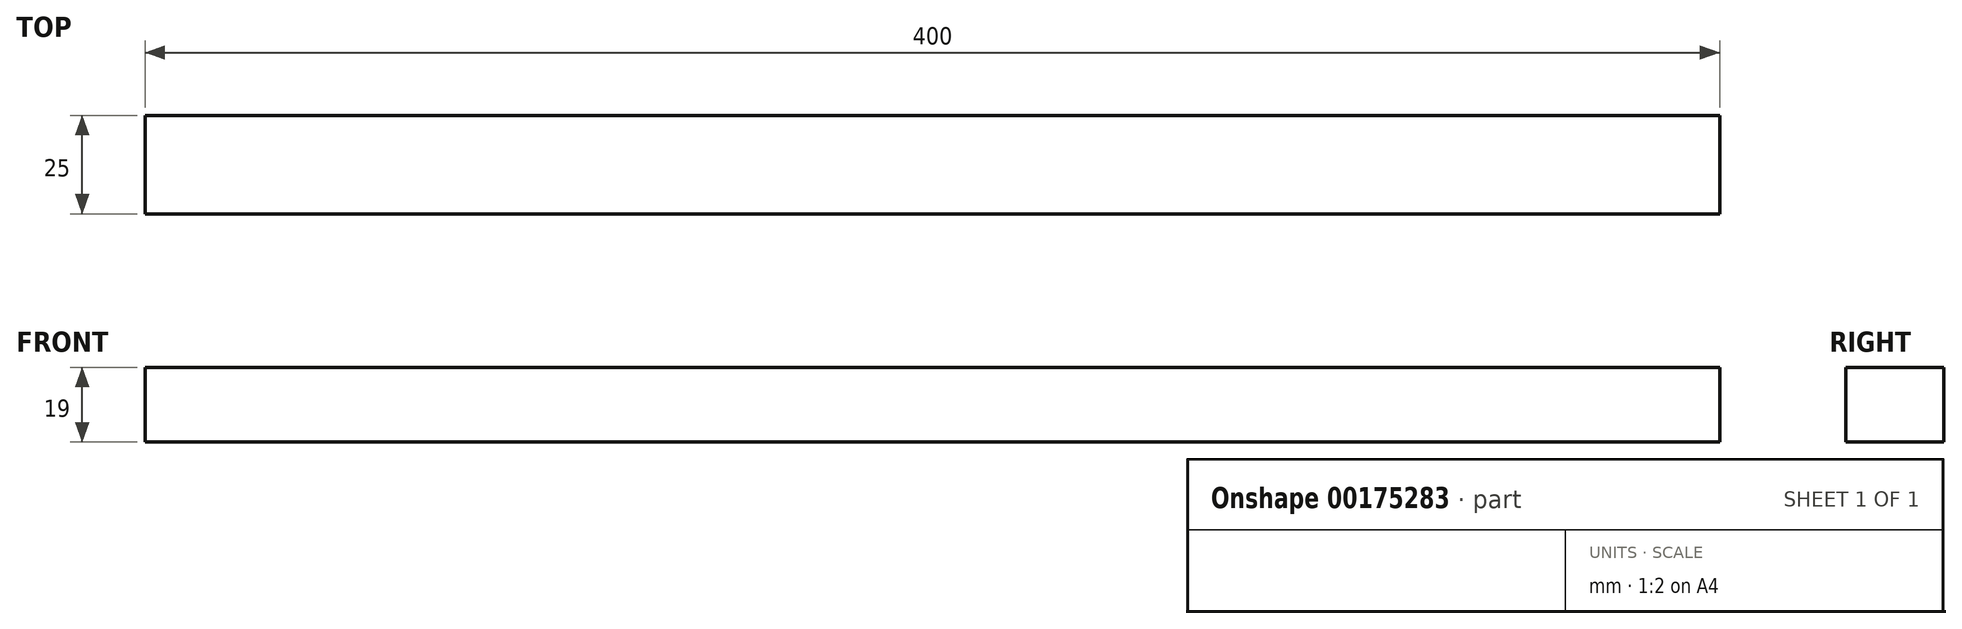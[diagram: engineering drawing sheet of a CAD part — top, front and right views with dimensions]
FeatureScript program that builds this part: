
annotation { "Feature Type Name" : "Feature", "Feature Type Description" : "" }
export const myFeature = defineFeature(function(context is Context, id is Id, definition is map)
    precondition{}
    {
        {
            var Q0;
            Q0=qCreatedBy(makeId("Front.planeOp"),FACE);
            var sketch = newSketch(context, id + "F0", { "sketchPlane" : qUnion([Q0])});
            skLineSegment(sketch, "E0.bottom", {"start": v(-200, 9.5) * mm, "end": v(200, 9.5) * mm});
            skLineSegment(sketch, "E0.top", {"start": v(-200, -9.5) * mm, "end": v(200, -9.5) * mm});
            skLineSegment(sketch, "E0.left", {"start": v(-200, 9.5) * mm, "end": v(-200, -9.5) * mm});
            skLineSegment(sketch, "E0.right", {"start": v(200, 9.5) * mm, "end": v(200, -9.5) * mm});
            skPoint(sketch, "E0.middle", {"position": v(0, 0) * mm});
            skSolve(sketch);
        }
        {
            var Q0;
            Q0=makeQuery(id+"F0.imprint","IMPRINT",FACE,{"disambiguationData":[TD([[makeQuery(id+"F0.imprint","IMPRINT",EDGE,{"derivedFrom":sQuery(id+"F0.wireOp",EDGE,"E0.bottom")}),-1.0]])]});
            extrude(context, id + "F1", {"entities" : qUnion([Q0]), "depth" : 25 * mm});
        }
    });
